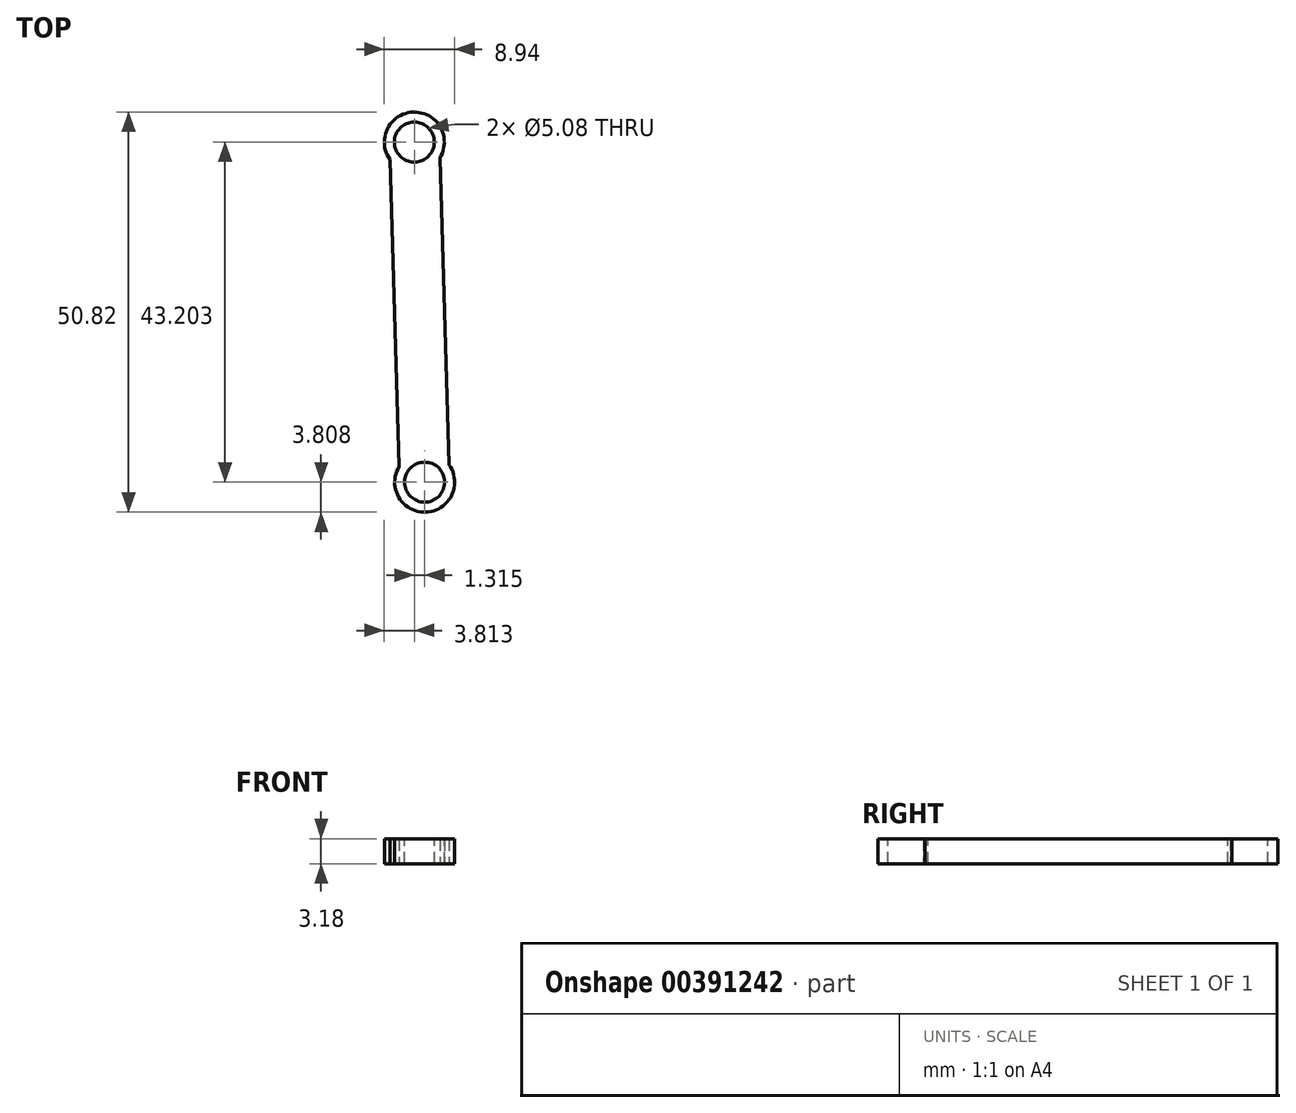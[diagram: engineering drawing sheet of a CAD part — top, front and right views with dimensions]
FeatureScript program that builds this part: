
annotation { "Feature Type Name" : "Feature", "Feature Type Description" : "" }
export const myFeature = defineFeature(function(context is Context, id is Id, definition is map)
    precondition{}
    {
        {
            var Q0;
            Q0=qCreatedBy(makeId("Top.planeOp"),FACE);
            var sketch = newSketch(context, id + "F0", { "sketchPlane" : qUnion([Q0])});
            skLineSegment(sketch, "E0.right", {"start": v(-2.58, -19.6) * mm, "end": v(-3.77, 19.4) * mm});
            skPoint(sketch, "E0.middle", {"position": v(0, 0) * mm});
            skArc(sketch, "E1", {"start": v(-2.58, -19.6) * mm, "mid": v(0.77, -25.4) * mm, "end": v(3.77, -19.4) * mm});
            skPoint(sketch, "E2.orphan", {"position": v(-2.52, -21.63) * mm});
            skPoint(sketch, "E3.orphan", {"position": v(3.83, -21.58) * mm});
            skPoint(sketch, "E4.orphan", {"position": v(-3.83, 21.58) * mm});
            skPoint(sketch, "E5.orphan", {"position": v(2.52, 21.63) * mm});
            skLineSegment(sketch, "E6", {"start": v(2.58, 19.6) * mm, "end": v(3.77, -19.4) * mm});
            skPoint(sketch, "E7.center.orphan", {"position": v(-0.66, 21.6) * mm});
            skArc(sketch, "E8", {"start": v(2.58, 19.6) * mm, "mid": v(-0.77, 25.4) * mm, "end": v(-3.77, 19.4) * mm});
            skSolve(sketch);
        }
        {
            var Q0;
            Q0=makeQuery(id+"F0.imprint","IMPRINT",FACE,{"disambiguationData":[TD([[makeQuery(id+"F0.imprint","IMPRINT",EDGE,{"derivedFrom":sQuery(id+"F0.wireOp",EDGE,"E0.left")}),1.0]])]});
            var Q1;
            Q1=makeQuery(id+"F0.imprint","IMPRINT",FACE,{"disambiguationData":[TD([[makeQuery(id+"F0.imprint","IMPRINT",EDGE,{"derivedFrom":sQuery(id+"F0.wireOp",EDGE,"E0.right")}),-1.0]])]});
            extrude(context, id + "F1", {"entities" : qUnion([Q0, Q1]), "depth" : 3.17 * mm});
        }
        {
            var Q0;
            Q0=makeQuery(id+"F1.opExtrude","CAP_FACE",FACE,{"disambiguationData":[OSD([sQuery(id+"F0.wireOp",EDGE,"E0.left"),sQuery(id+"F0.wireOp",EDGE,"E0.right"),sQuery(id+"F0.wireOp",EDGE,"E1"),sQuery(id+"F0.wireOp",EDGE,"E7")])],"isStart":false});
            var sketch = newSketch(context, id + "F2", { "sketchPlane" : qUnion([Q0])});
            skCircle(sketch, "E9", {"center": v(0.66, -21.6) * mm, "radius": 2.54 * mm});
            skCircle(sketch, "E10", {"center": v(-0.66, 21.6) * mm, "radius": 2.54 * mm});
            skSolve(sketch);
        }
        {
            var Q0;
            Q0=sQuery(id+"F2.wireOp",VERTEX,"E9.center");
            var Q1;
            Q1=sQuery(id+"F2.wireOp",VERTEX,"E10.center");
            var Q2;
            Q2=makeQuery(id+"F1.opExtrude","SWEPT_BODY",BODY,{"disambiguationData":[OSD([sQuery(id+"F0.wireOp",EDGE,"E0.left"),sQuery(id+"F0.wireOp",EDGE,"E0.right"),sQuery(id+"F0.wireOp",EDGE,"E1"),sQuery(id+"F0.wireOp",EDGE,"E7")])]});
            hole(context, id + "F3", {"style" : HoleStyle.SIMPLE, "endStyle" : HoleEndStyle.THROUGH, "holeDiameter" : 5.08 * mm, "isTappedThrough" : true, "tappedDepth" : 12.7 * mm, "tapClearance" : 3, "locations" : qUnion([Q0, Q1]), "scope" : qUnion([Q2])});
        }
    });
